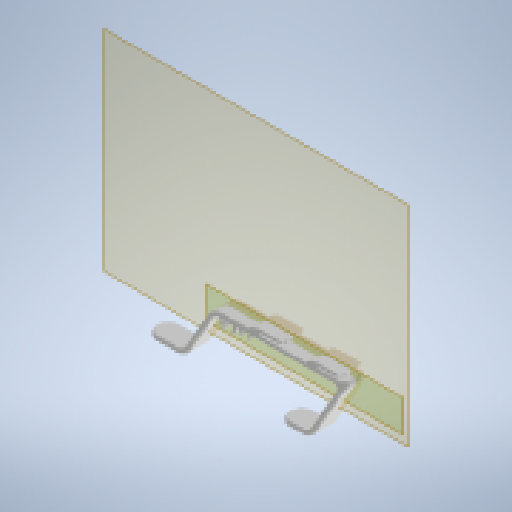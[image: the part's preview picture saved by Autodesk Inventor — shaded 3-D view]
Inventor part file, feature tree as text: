
AUTODESK INVENTOR PART (.ipt)
format: ipt  version: 2024.1 (Build 281209000, 209)  size: 893,440 bytes
history: native  units: mm
features: fillet x10, chamfer x6, other x4, extrude x3, projected_geometry x3, plane x2, sketch x1, reference x1
ambient origin geometry x8: Origin, YZ Plane, XZ Plane, XY Plane, X Axis, Y Axis, Z Axis, Center Point
bodies: Body1 (feature_tree)
feature tree (30):
  other  "cable-hanger"
  extrude  "Extrusion1"  Depth=3.0mm
  fillet  "Fillet1"  Radius=10.0mm
  fillet  "Fillet2"  Radius=1.0mm
  chamfer  "Chamfer8"  Distance=6.0mm
  fillet  "Fillet8"  Radius=8.0mm
  fillet  "Fillet17"  Radius=1.2mm
  chamfer  "Chamfer1"  Distance=1.4mm
  plane  "Work Plane1"
  extrude  "Extrusion2"  Depth=3.0mm
  fillet  "Fillet3"  Radius=1.5mm
  fillet  "Fillet4"  Radius=4.0mm
  chamfer  "Chamfer2"  Distance=2.0mm
  plane  "Work Plane2"
  fillet  "Fillet9"  Radius=8.0mm
  extrude  "Extrusion3"  Depth=3.0mm
  chamfer  "Chamfer3"  Distance=1.0mm
  chamfer  "Chamfer4"  Distance=1.0mm Angle=45.0deg
  fillet  "Fillet10"  Radius=3.0mm
  chamfer  "Chamfer5"  Distance=8.0mm
  fillet  "Fillet12"  Radius=0.8mm
  fillet  "Fillet13"  Radius=0.5mm
  sketch  "Sketch2"  dims[d14=15.0mm d15=0.0mm d16=7.5mm d17=10.0mm d18=1.0mm d19=2.0mm d20=45.0deg d54=6.0mm d55=8.0mm d60=1.2mm d61=1.2mm d62=1.4mm d65=3.0mm d66=1.5mm d67=4.0mm d68=2.0mm d69=8.0mm d70=0.0mm d71=1.0mm d72=1.0mm d73=1.0mm d74=2.0mm d75=45.0deg d76=3.0mm d78=8.0mm d79=0.0mm d80=0.8mm d81=2.0mm d82=45.0deg d83=0.5mm d84=2.0mm d85=45.0deg d96=0.5mm d97=2.0mm d98=45.0deg d131=3.0mm d132=2.0mm d133=45.0deg d134=2.0mm d136=6.0mm d137=5.0mm d138=11.0mm d139=4.0mm d140=13.0mm d143=0.7mm d145=0.7mm d153=13.0mm d154=3.0mm d159=12.011689mm d160=7.0mm d161=15.0mm d162=37.0mm d163=7.0mm d164=15.0mm d165=1.5mm d166=2.0mm d167=3.0mm d168=2.8mm d169=35.0mm d170=3.0mm d171=15.0mm d172=25.0mm d173=3.0mm d174=60.0deg d175=3.0mm d176=20.0mm d178=60.0deg d179=60.0deg d181=3.0mm d182=30.0mm d184=80.0mm d189=6.5mm d190=5.803848mm]
  projected_geometry  "Projected Loop2"
  projected_geometry  "Projected Loop3"
  projected_geometry  "Projected Loop4"
  reference  "Reference3"
  other  "<userpath>\Documents\0004-CAD\3D-cad-main\cable-hanger\VERSION3-largel-upright-hook.iam"
  other  "VERSION3-largel-upright-hook.iam"
  other  "backplate-0:1"
